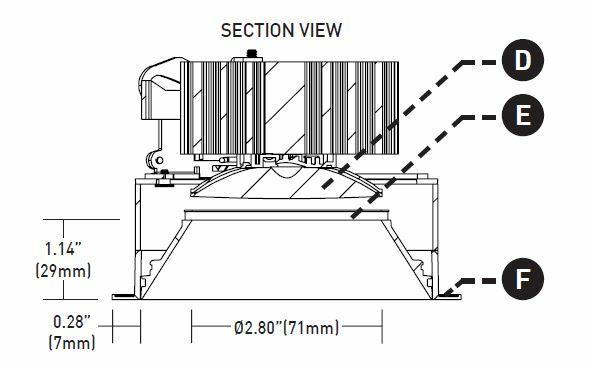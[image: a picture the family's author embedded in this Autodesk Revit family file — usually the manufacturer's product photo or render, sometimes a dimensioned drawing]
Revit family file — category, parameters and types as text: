
# Revit family: Lighting-Surface-Lucifer-Cylinder-CY3
name_source: partatom
category: Lighting Fixtures
revit_build: Autodesk Revit 2016 (Build: 20170117_1200(x64)
units: mm (PartAtom-declared; Revit-internal decimal feet)

## family parameters
Cut with Voids When Loaded = No
Host = Face
Light Source = Yes
Part Type = Normal
Room Calculation Point = No
Round Connector Dimension = Use Diameter
Shared = No

## types (1)
- CY3-FB
    Apparent Load = 0 VA
    Color Filter = 16777215
    Default Elevation = 48 "
    Description = Fixed Surface Mount
    Dimming Lamp Color Temperature Shift = <None>
    Emit Shape Visible in Rendering = No
    Emit from Circle Diameter = 3.25 "
    Lamp = LED
    Manufacturer = Lucifer Lighting
    Model = CY3-FB
    Number of Poles = 1
    Photometric Web File = Load File
    Power Factor = 1
    Tilt Angle = -90.00°
    URL = https://www.luciferlighting.com
    Voltage = 0 V

## geometry (parser evidence)
native form markers: Sweep x3
no freeform markers — native parametric forms only
